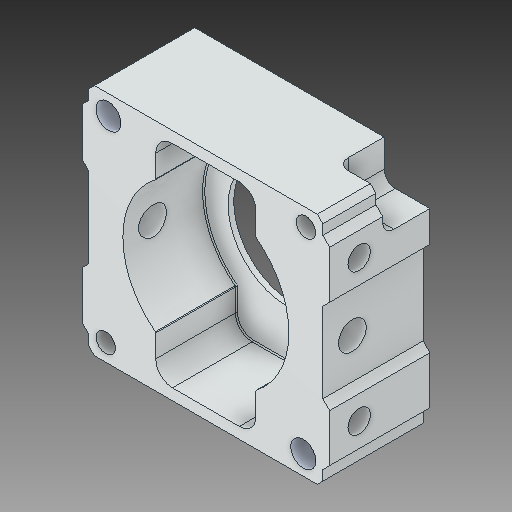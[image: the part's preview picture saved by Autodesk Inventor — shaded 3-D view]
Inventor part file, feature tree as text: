
AUTODESK INVENTOR PART (.ipt)
format: ipt  version: 2018 (Build 220112000, 112)  size: 267,776 bytes
history: native  units: in
note: dims shown in document units (in); Inventor stores cm internally (conversion verified against a paired STEP export)
features: chamfer x1
ambient origin geometry x8: Origin, YZ Plane, XZ Plane, XY Plane, X Axis, Y Axis, Z Axis, Center Point
bodies: Solid1 (feature_tree)
feature tree (1):
  chamfer  "Chamfer4"  [1 undecoded]
note: 1 required parameter value undecoded (feature->parameter linkage not recoverable at this tier; creation-order binding heuristic only, values carry confidence <= 0.55)
